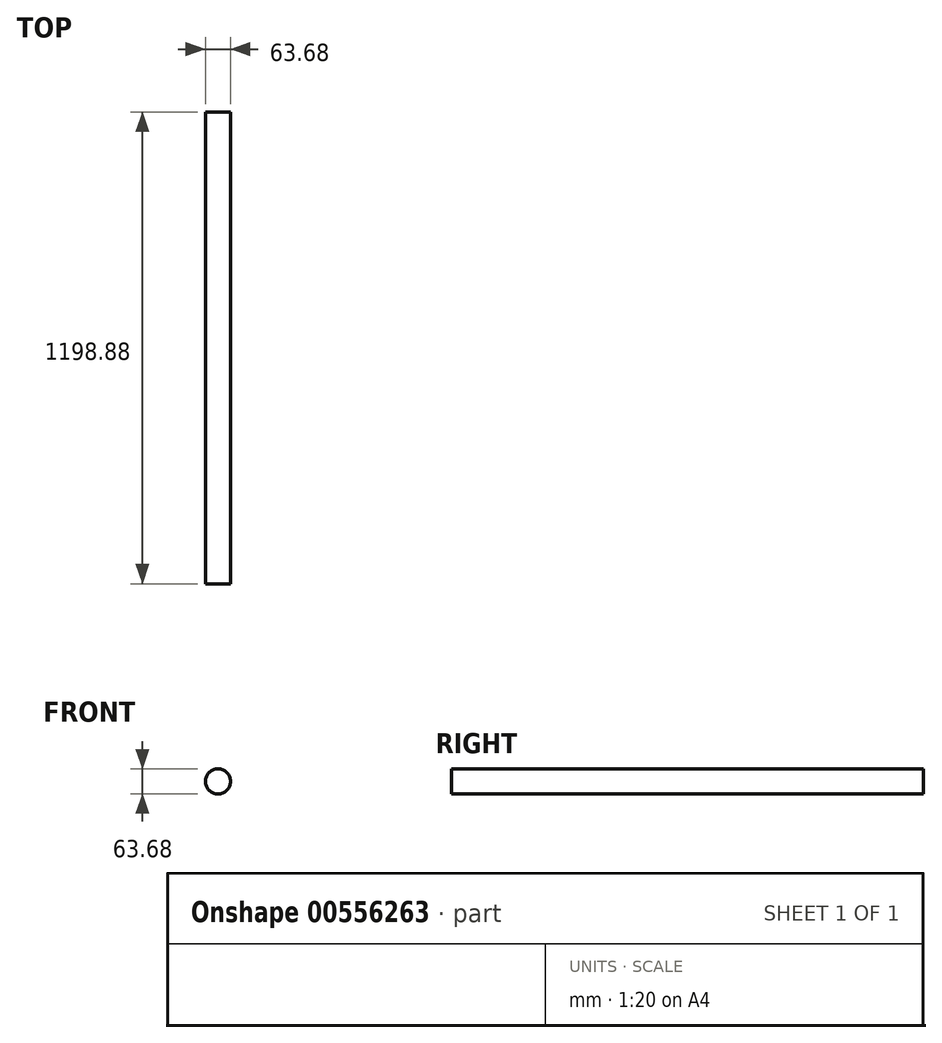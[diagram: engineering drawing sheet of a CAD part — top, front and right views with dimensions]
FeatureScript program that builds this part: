
annotation { "Feature Type Name" : "Feature", "Feature Type Description" : "" }
export const myFeature = defineFeature(function(context is Context, id is Id, definition is map)
    precondition{}
    {
        {
            var Q0;
            Q0=qCreatedBy(makeId("Front.planeOp"),FACE);
            var sketch = newSketch(context, id + "F0", { "sketchPlane" : qUnion([Q0])});
            skCircle(sketch, "E0", {"center": v(0, 0) * mm, "radius": 31.84 * mm});
            skSolve(sketch);
        }
        {
            var Q0;
            Q0 = qSketchRegion(id + "F0", true);
            extrude(context, id + "F1", {"entities" : qUnion([Q0]), "depth" : 1198.88 * mm, "offsetDistance" : 25.4 * mm});
        }
    });
